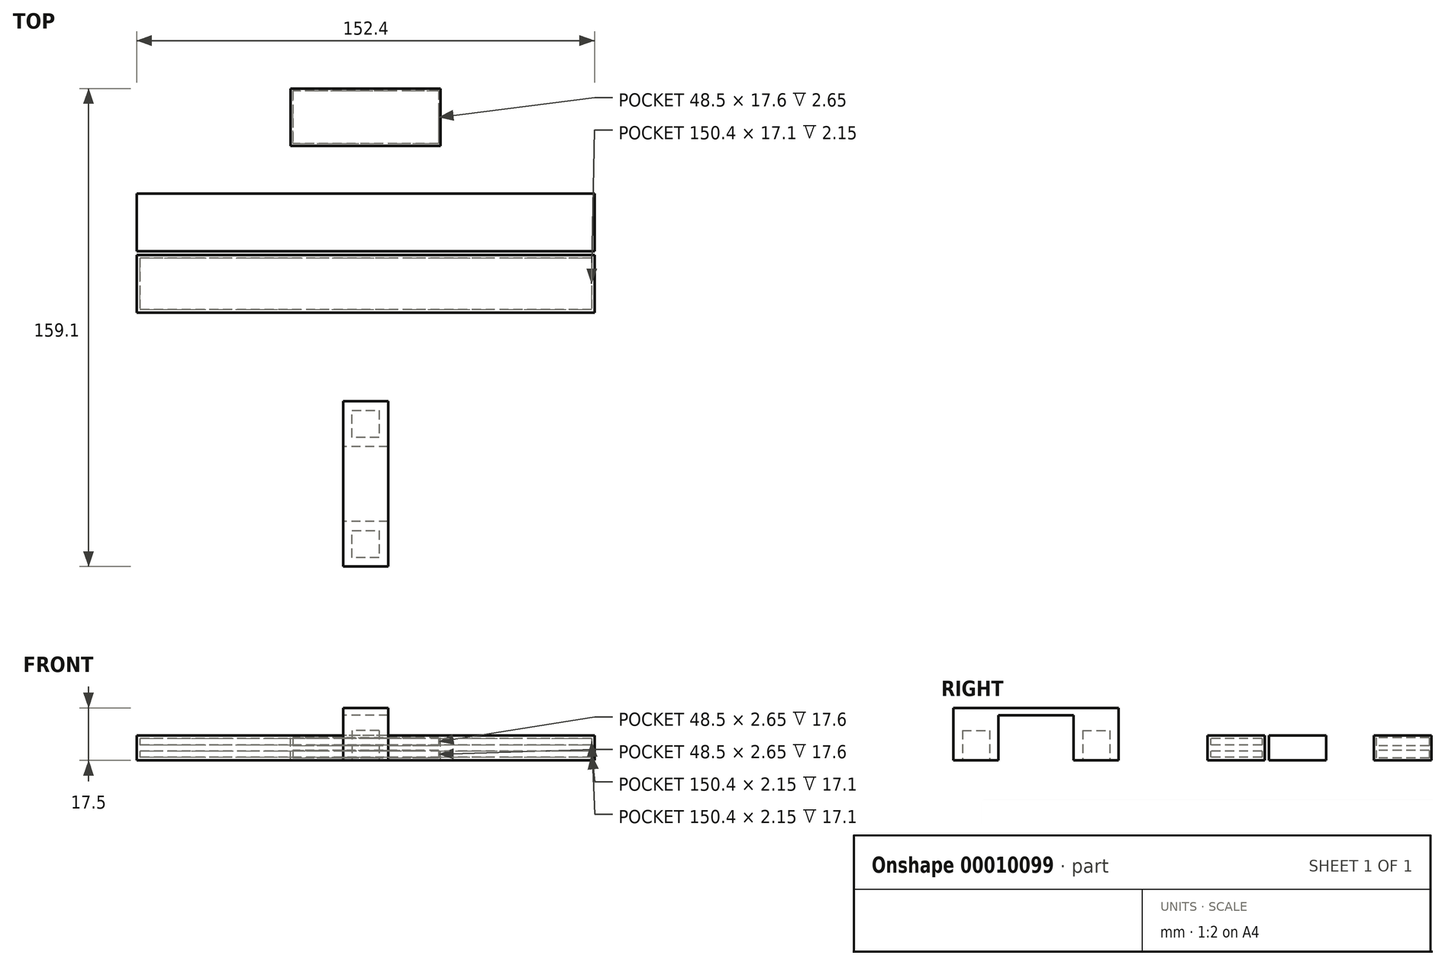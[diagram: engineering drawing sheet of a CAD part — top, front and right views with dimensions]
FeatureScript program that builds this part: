
annotation { "Feature Type Name" : "Feature", "Feature Type Description" : "" }
export const myFeature = defineFeature(function(context is Context, id is Id, definition is map)
    precondition{}
    {
        {
            var Q0;
            Q0=qCreatedBy(makeId("Right.planeOp"),FACE);
            var sketch = newSketch(context, id + "F0", { "sketchPlane" : qUnion([Q0])});
            skLineSegment(sketch, "E0.bottom", {"start": v(0, 0) * mm, "end": v(19.1, 0) * mm});
            skLineSegment(sketch, "E0.top", {"start": v(0, 8.3) * mm, "end": v(19.1, 8.3) * mm});
            skLineSegment(sketch, "E0.left", {"start": v(0, 0) * mm, "end": v(0, 8.3) * mm});
            skLineSegment(sketch, "E0.right", {"start": v(19.1, 0) * mm, "end": v(19.1, 8.3) * mm});
            skSolve(sketch);
        }
        {
            var Q0;
            Q0=makeQuery(id+"F0.imprint","IMPRINT",FACE,{"disambiguationData":[TD([[makeQuery(id+"F0.imprint","IMPRINT",EDGE,{"derivedFrom":sQuery(id+"F0.wireOp",EDGE,"E0.bottom")}),1.0]])]});
            extrude(context, id + "F1", {"entities" : qUnion([Q0]), "endBound" : BoundingType.SYMMETRIC, "depth" : 152.4 * mm});
        }
        {
            var Q0;
            Q0=qCreatedBy(makeId("Right.planeOp"),FACE);
            var sketch = newSketch(context, id + "F2", { "sketchPlane" : qUnion([Q0])});
            skLineSegment(sketch, "E1.bottom", {"start": v(-1.32, 0) * mm, "end": v(-20.42, 0) * mm});
            skLineSegment(sketch, "E1.top", {"start": v(-1.32, 8.3) * mm, "end": v(-20.42, 8.3) * mm});
            skLineSegment(sketch, "E1.left", {"start": v(-1.32, 0) * mm, "end": v(-1.32, 8.3) * mm});
            skLineSegment(sketch, "E1.right", {"start": v(-20.42, 0) * mm, "end": v(-20.42, 8.3) * mm});
            skLineSegment(sketch, "E2.bottom", {"start": v(-2.32, 7.3) * mm, "end": v(-19.42, 7.3) * mm});
            skLineSegment(sketch, "E2.top", {"start": v(-2.32, 1) * mm, "end": v(-19.42, 1) * mm});
            skLineSegment(sketch, "E2.left", {"start": v(-2.32, 7.3) * mm, "end": v(-2.32, 5.15) * mm});
            skLineSegment(sketch, "E2.right", {"start": v(-19.42, 7.3) * mm, "end": v(-19.42, 5.15) * mm});
            skLineSegment(sketch, "E3", {"start": v(-2.32, 5.15) * mm, "end": v(-19.42, 5.15) * mm});
            skLineSegment(sketch, "E4", {"start": v(-2.32, 3.15) * mm, "end": v(-19.42, 3.15) * mm});
            skLineSegment(sketch, "E5.trimOffspring", {"start": v(-2.32, 3.15) * mm, "end": v(-2.32, 1) * mm});
            skLineSegment(sketch, "E6.trimOffspring", {"start": v(-19.42, 3.15) * mm, "end": v(-19.42, 1) * mm});
            skSolve(sketch);
        }
        {
            var Q0;
            Q0=makeQuery(id+"F2.imprint","IMPRINT",FACE,{"disambiguationData":[TD([[makeQuery(id+"F2.imprint","IMPRINT",EDGE,{"derivedFrom":sQuery(id+"F2.wireOp",EDGE,"E1.bottom")}),-1.0]])]});
            extrude(context, id + "F3", {"entities" : qUnion([Q0]), "endBound" : BoundingType.SYMMETRIC, "depth" : 150.4 * mm});
        }
        {
            var Q0;
            Q0=makeQuery(id+"F3.opExtrude","CAP_FACE",FACE,{"disambiguationData":[OSD([sQuery(id+"F2.wireOp",EDGE,"E1.bottom"),sQuery(id+"F2.wireOp",EDGE,"E1.top"),sQuery(id+"F2.wireOp",EDGE,"E1.left"),sQuery(id+"F2.wireOp",EDGE,"E1.right"),sQuery(id+"F2.wireOp",EDGE,"E2.bottom"),sQuery(id+"F2.wireOp",EDGE,"E2.top"),sQuery(id+"F2.wireOp",EDGE,"E2.left"),sQuery(id+"F2.wireOp",EDGE,"E2.right"),sQuery(id+"F2.wireOp",EDGE,"E3"),sQuery(id+"F2.wireOp",EDGE,"E4"),sQuery(id+"F2.wireOp",EDGE,"E5.trimOffspring"),sQuery(id+"F2.wireOp",EDGE,"E6.trimOffspring")])],"isStart":true});
            var sketch = newSketch(context, id + "F4", { "sketchPlane" : qUnion([Q0])});
            skSolve(sketch);
        }
        {
            var Q0;
            Q0=makeQuery(id+"F4.imprint","IMPRINT",FACE,{"disambiguationData":[TD([[makeQuery(id+"F4.imprint","IMPRINT",EDGE,{"derivedFrom":makeQuery(id+"F3.opExtrude","CAP_EDGE",EDGE,{"disambiguationData":[OSD([sQuery(id+"F2.wireOp",EDGE,"E1.bottom")])],"isStart":true})}),1.0]])]});
            var Q1;
            Q1=makeQuery(id+"F4.imprint","IMPRINT",FACE,{"disambiguationData":[TD([[makeQuery(id+"F4.imprint","IMPRINT",EDGE,{"derivedFrom":makeQuery(id+"F3.opExtrude","CAP_EDGE",EDGE,{"disambiguationData":[OSD([sQuery(id+"F2.wireOp",EDGE,"E2.bottom")])],"isStart":true})}),-1.0]])]});
            var Q2;
            Q2=makeQuery(id+"F4.imprint","IMPRINT",FACE,{"disambiguationData":[TD([[makeQuery(id+"F4.imprint","IMPRINT",EDGE,{"derivedFrom":makeQuery(id+"F3.opExtrude","CAP_EDGE",EDGE,{"disambiguationData":[OSD([sQuery(id+"F2.wireOp",EDGE,"E2.top")])],"isStart":true})}),1.0]])]});
            extrude(context, id + "F5", {"entities" : qUnion([Q0, Q1, Q2]), "operationType" : NewBodyOperationType.ADD, "depth" : 1 * mm});
        }
        {
            var Q0;
            Q0=makeQuery(id+"F3.opExtrude","CAP_FACE",FACE,{"disambiguationData":[OSD([sQuery(id+"F2.wireOp",EDGE,"E1.bottom"),sQuery(id+"F2.wireOp",EDGE,"E1.top"),sQuery(id+"F2.wireOp",EDGE,"E1.left"),sQuery(id+"F2.wireOp",EDGE,"E1.right"),sQuery(id+"F2.wireOp",EDGE,"E2.bottom"),sQuery(id+"F2.wireOp",EDGE,"E2.top"),sQuery(id+"F2.wireOp",EDGE,"E2.left"),sQuery(id+"F2.wireOp",EDGE,"E2.right"),sQuery(id+"F2.wireOp",EDGE,"E3"),sQuery(id+"F2.wireOp",EDGE,"E4"),sQuery(id+"F2.wireOp",EDGE,"E5.trimOffspring"),sQuery(id+"F2.wireOp",EDGE,"E6.trimOffspring")])],"isStart":false});
            var sketch = newSketch(context, id + "F6", { "sketchPlane" : qUnion([Q0])});
            skSolve(sketch);
        }
        {
            var Q0;
            Q0=makeQuery(id+"F6.imprint","IMPRINT",FACE,{"disambiguationData":[TD([[makeQuery(id+"F6.imprint","IMPRINT",EDGE,{"derivedFrom":makeQuery(id+"F3.opExtrude","CAP_EDGE",EDGE,{"disambiguationData":[OSD([sQuery(id+"F2.wireOp",EDGE,"E1.bottom")])],"isStart":false})}),-1.0]])]});
            var Q1;
            Q1=makeQuery(id+"F6.imprint","IMPRINT",FACE,{"disambiguationData":[TD([[makeQuery(id+"F6.imprint","IMPRINT",EDGE,{"derivedFrom":makeQuery(id+"F3.opExtrude","CAP_EDGE",EDGE,{"disambiguationData":[OSD([sQuery(id+"F2.wireOp",EDGE,"E2.top")])],"isStart":false})}),-1.0]])]});
            var Q2;
            Q2=makeQuery(id+"F6.imprint","IMPRINT",FACE,{"disambiguationData":[TD([[makeQuery(id+"F6.imprint","IMPRINT",EDGE,{"derivedFrom":makeQuery(id+"F3.opExtrude","CAP_EDGE",EDGE,{"disambiguationData":[OSD([sQuery(id+"F2.wireOp",EDGE,"E2.bottom")])],"isStart":false})}),1.0]])]});
            extrude(context, id + "F7", {"entities" : qUnion([Q0, Q1, Q2]), "operationType" : NewBodyOperationType.ADD, "depth" : 1 * mm});
        }
        {
            var Q0;
            Q0=qCreatedBy(makeId("Right.planeOp"),FACE);
            var sketch = newSketch(context, id + "F8", { "sketchPlane" : qUnion([Q0])});
            skLineSegment(sketch, "E7", {"start": v(0, 0) * mm, "end": v(35, 0) * mm, "construction": true});
            skLineSegment(sketch, "E8.bottom", {"start": v(35, 0) * mm, "end": v(54.1, 0) * mm});
            skLineSegment(sketch, "E8.top", {"start": v(35, 8.3) * mm, "end": v(54.1, 8.3) * mm});
            skLineSegment(sketch, "E8.left", {"start": v(35, 0) * mm, "end": v(35, 8.3) * mm});
            skLineSegment(sketch, "E8.right", {"start": v(54.1, 0) * mm, "end": v(54.1, 8.3) * mm});
            skLineSegment(sketch, "E9.bottom", {"start": v(53.35, 7.55) * mm, "end": v(35.75, 7.55) * mm});
            skLineSegment(sketch, "E9.top", {"start": v(53.35, 0.75) * mm, "end": v(35.75, 0.75) * mm});
            skLineSegment(sketch, "E9.left", {"start": v(53.35, 7.55) * mm, "end": v(53.35, 4.9) * mm});
            skLineSegment(sketch, "E9.right", {"start": v(35.75, 7.55) * mm, "end": v(35.75, 4.9) * mm});
            skLineSegment(sketch, "E10", {"start": v(53.35, 4.9) * mm, "end": v(35.75, 4.9) * mm});
            skLineSegment(sketch, "E11", {"start": v(53.35, 4.15) * mm, "end": v(35.75, 4.15) * mm, "construction": true});
            skLineSegment(sketch, "E12", {"start": v(53.35, 3.4) * mm, "end": v(35.75, 3.4) * mm});
            skLineSegment(sketch, "E13.trimOffspring", {"start": v(35.75, 3.4) * mm, "end": v(35.75, 0.75) * mm});
            skLineSegment(sketch, "E14.trimOffspring", {"start": v(53.35, 3.4) * mm, "end": v(53.35, 0.75) * mm});
            skSolve(sketch);
        }
        {
            var Q0;
            Q0=makeQuery(id+"F8.imprint","IMPRINT",FACE,{"disambiguationData":[TD([[makeQuery(id+"F8.imprint","IMPRINT",EDGE,{"derivedFrom":sQuery(id+"F8.wireOp",EDGE,"E8.bottom")}),1.0]])]});
            extrude(context, id + "F9", {"entities" : qUnion([Q0]), "endBound" : BoundingType.SYMMETRIC, "depth" : 48.5 * mm});
        }
        {
            var Q0;
            Q0=makeQuery(id+"F9.opExtrude","CAP_FACE",FACE,{"disambiguationData":[OSD([sQuery(id+"F8.wireOp",EDGE,"E8.bottom"),sQuery(id+"F8.wireOp",EDGE,"E8.top"),sQuery(id+"F8.wireOp",EDGE,"E8.left"),sQuery(id+"F8.wireOp",EDGE,"E8.right"),sQuery(id+"F8.wireOp",EDGE,"E9.bottom"),sQuery(id+"F8.wireOp",EDGE,"E9.top"),sQuery(id+"F8.wireOp",EDGE,"E9.left"),sQuery(id+"F8.wireOp",EDGE,"E9.right"),sQuery(id+"F8.wireOp",EDGE,"E10"),sQuery(id+"F8.wireOp",EDGE,"E12"),sQuery(id+"F8.wireOp",EDGE,"E13.trimOffspring"),sQuery(id+"F8.wireOp",EDGE,"E14.trimOffspring")])],"isStart":true});
            var sketch = newSketch(context, id + "F10", { "sketchPlane" : qUnion([Q0])});
            skLineSegment(sketch, "E15.bottom", {"start": v(-54.1, 8.3) * mm, "end": v(-35, 8.3) * mm});
            skLineSegment(sketch, "E15.top", {"start": v(-54.1, 0) * mm, "end": v(-35, 0) * mm});
            skLineSegment(sketch, "E15.left", {"start": v(-54.1, 8.3) * mm, "end": v(-54.1, 0) * mm});
            skLineSegment(sketch, "E15.right", {"start": v(-35, 8.3) * mm, "end": v(-35, 0) * mm});
            skSolve(sketch);
        }
        {
            var Q0;
            Q0=makeQuery(id+"F10.imprint","IMPRINT",FACE,{"disambiguationData":[TD([[makeQuery(id+"F10.imprint","IMPRINT",EDGE,{"derivedFrom":sQuery(id+"F10.wireOp",EDGE,"E15.bottom")}),1.0]])]});
            var Q1;
            Q1=makeQuery(id+"F10.imprint","IMPRINT",FACE,{"disambiguationData":[TD([[makeQuery(id+"F10.imprint","IMPRINT",EDGE,{"derivedFrom":makeQuery(id+"F9.opExtrude","CAP_EDGE",EDGE,{"disambiguationData":[OSD([sQuery(id+"F8.wireOp",EDGE,"E9.bottom")])],"isStart":true})}),-1.0]])]});
            var Q2;
            Q2=makeQuery(id+"F10.imprint","IMPRINT",FACE,{"disambiguationData":[TD([[makeQuery(id+"F10.imprint","IMPRINT",EDGE,{"derivedFrom":makeQuery(id+"F9.opExtrude","CAP_EDGE",EDGE,{"disambiguationData":[OSD([sQuery(id+"F8.wireOp",EDGE,"E9.top")])],"isStart":true})}),1.0]])]});
            extrude(context, id + "F11", {"entities" : qUnion([Q0, Q1, Q2]), "operationType" : NewBodyOperationType.ADD, "depth" : 0.75 * mm});
        }
        {
            var Q0;
            Q0=makeQuery(id+"F9.opExtrude","CAP_FACE",FACE,{"disambiguationData":[OSD([sQuery(id+"F8.wireOp",EDGE,"E8.bottom"),sQuery(id+"F8.wireOp",EDGE,"E8.top"),sQuery(id+"F8.wireOp",EDGE,"E8.left"),sQuery(id+"F8.wireOp",EDGE,"E8.right"),sQuery(id+"F8.wireOp",EDGE,"E9.bottom"),sQuery(id+"F8.wireOp",EDGE,"E9.top"),sQuery(id+"F8.wireOp",EDGE,"E9.left"),sQuery(id+"F8.wireOp",EDGE,"E9.right"),sQuery(id+"F8.wireOp",EDGE,"E10"),sQuery(id+"F8.wireOp",EDGE,"E12"),sQuery(id+"F8.wireOp",EDGE,"E13.trimOffspring"),sQuery(id+"F8.wireOp",EDGE,"E14.trimOffspring")])],"isStart":false});
            var sketch = newSketch(context, id + "F12", { "sketchPlane" : qUnion([Q0])});
            skLineSegment(sketch, "E16.bottom", {"start": v(35, 8.3) * mm, "end": v(54.1, 8.3) * mm});
            skLineSegment(sketch, "E16.top", {"start": v(35, 0) * mm, "end": v(54.1, 0) * mm});
            skLineSegment(sketch, "E16.left", {"start": v(35, 8.3) * mm, "end": v(35, 0) * mm});
            skLineSegment(sketch, "E16.right", {"start": v(54.1, 8.3) * mm, "end": v(54.1, 0) * mm});
            skSolve(sketch);
        }
        {
            var Q0;
            Q0=makeQuery(id+"F12.imprint","IMPRINT",FACE,{"disambiguationData":[TD([[makeQuery(id+"F12.imprint","IMPRINT",EDGE,{"derivedFrom":sQuery(id+"F12.wireOp",EDGE,"E16.bottom")}),-1.0]])]});
            var Q1;
            Q1=makeQuery(id+"F12.imprint","IMPRINT",FACE,{"disambiguationData":[TD([[makeQuery(id+"F12.imprint","IMPRINT",EDGE,{"derivedFrom":makeQuery(id+"F9.opExtrude","CAP_EDGE",EDGE,{"disambiguationData":[OSD([sQuery(id+"F8.wireOp",EDGE,"E9.bottom")])],"isStart":false})}),1.0]])]});
            var Q2;
            Q2=makeQuery(id+"F12.imprint","IMPRINT",FACE,{"disambiguationData":[TD([[makeQuery(id+"F12.imprint","IMPRINT",EDGE,{"derivedFrom":makeQuery(id+"F9.opExtrude","CAP_EDGE",EDGE,{"disambiguationData":[OSD([sQuery(id+"F8.wireOp",EDGE,"E9.top")])],"isStart":false})}),-1.0]])]});
            extrude(context, id + "F13", {"entities" : qUnion([Q0, Q1, Q2]), "operationType" : NewBodyOperationType.ADD, "depth" : 0.75 * mm});
        }
        {
            var Q0;
            Q0=qCreatedBy(makeId("Right.planeOp"),FACE);
            var sketch = newSketch(context, id + "F14", { "sketchPlane" : qUnion([Q0])});
            skLineSegment(sketch, "E17", {"start": v(0, 0) * mm, "end": v(-50, 0) * mm, "construction": true});
            skLineSegment(sketch, "E18.bottom", {"start": v(-50, 0) * mm, "end": v(-65, 0) * mm});
            skLineSegment(sketch, "E18.top", {"start": v(-50, 15) * mm, "end": v(-65, 15) * mm});
            skLineSegment(sketch, "E18.left", {"start": v(-50, 0) * mm, "end": v(-50, 15) * mm});
            skLineSegment(sketch, "E18.right", {"start": v(-65, 0) * mm, "end": v(-65, 15) * mm});
            skLineSegment(sketch, "E19", {"start": v(-65, 15) * mm, "end": v(-90, 15) * mm});
            skLineSegment(sketch, "E20.bottom", {"start": v(-90, 15) * mm, "end": v(-105, 15) * mm});
            skLineSegment(sketch, "E20.top", {"start": v(-90, 0) * mm, "end": v(-105, 0) * mm});
            skLineSegment(sketch, "E20.left", {"start": v(-90, 15) * mm, "end": v(-90, 0) * mm});
            skLineSegment(sketch, "E20.right", {"start": v(-105, 15) * mm, "end": v(-105, 0) * mm});
            skLineSegment(sketch, "E21.bottom", {"start": v(-105, 15) * mm, "end": v(-50, 15) * mm});
            skLineSegment(sketch, "E21.top", {"start": v(-105, 17.5) * mm, "end": v(-50, 17.5) * mm});
            skLineSegment(sketch, "E21.left", {"start": v(-105, 15) * mm, "end": v(-105, 17.5) * mm});
            skLineSegment(sketch, "E21.right", {"start": v(-50, 15) * mm, "end": v(-50, 17.5) * mm});
            skSolve(sketch);
        }
        {
            var Q0;
            Q0=makeQuery(id+"F14.imprint","IMPRINT",FACE,{"disambiguationData":[TD([[makeQuery(id+"F14.imprint","IMPRINT",EDGE,{"derivedFrom":sQuery(id+"F14.wireOp",EDGE,"E20.top")}),-1.0]])]});
            var Q1;
            Q1=makeQuery(id+"F14.imprint","IMPRINT",FACE,{"disambiguationData":[TD([[makeQuery(id+"F14.imprint","IMPRINT",EDGE,{"derivedFrom":sQuery(id+"F14.wireOp",EDGE,"E21.top")}),-1.0]])]});
            var Q2;
            Q2=makeQuery(id+"F14.imprint","IMPRINT",FACE,{"disambiguationData":[TD([[makeQuery(id+"F14.imprint","IMPRINT",EDGE,{"derivedFrom":sQuery(id+"F14.wireOp",EDGE,"E18.bottom")}),-1.0]])]});
            extrude(context, id + "F15", {"entities" : qUnion([Q0, Q1, Q2]), "endBound" : BoundingType.SYMMETRIC, "depth" : 15 * mm});
        }
        {
            var Q0;
            Q0=makeQuery(id+"F15.opExtrude","SWEPT_FACE",FACE,{"disambiguationData":[OSD([sQuery(id+"F14.wireOp",EDGE,"E20.top")])]});
            var sketch = newSketch(context, id + "F16", { "sketchPlane" : qUnion([Q0])});
            skLineSegment(sketch, "E22.0.0", {"start": v(-7.5, 105) * mm, "end": v(-7.5, 90) * mm});
            skLineSegment(sketch, "E22.0.1", {"start": v(-7.5, 90) * mm, "end": v(7.5, 90) * mm});
            skLineSegment(sketch, "E22.0.2", {"start": v(7.5, 90) * mm, "end": v(7.5, 105) * mm});
            skLineSegment(sketch, "E22.0.3", {"start": v(7.5, 105) * mm, "end": v(-7.5, 105) * mm});
            skLineSegment(sketch, "E23.0.0", {"start": v(-7.5, 65) * mm, "end": v(-7.5, 50) * mm});
            skLineSegment(sketch, "E23.0.1", {"start": v(-7.5, 50) * mm, "end": v(7.5, 50) * mm});
            skLineSegment(sketch, "E23.0.2", {"start": v(7.5, 50) * mm, "end": v(7.5, 65) * mm});
            skLineSegment(sketch, "E23.0.3", {"start": v(7.5, 65) * mm, "end": v(-7.5, 65) * mm});
            skLineSegment(sketch, "E24.0", {"start": v(-4.5, 102) * mm, "end": v(-4.5, 93) * mm});
            skLineSegment(sketch, "E24.1", {"start": v(4.5, 102) * mm, "end": v(-4.5, 102) * mm});
            skLineSegment(sketch, "E24.2", {"start": v(4.5, 93) * mm, "end": v(4.5, 102) * mm});
            skLineSegment(sketch, "E24.3", {"start": v(-4.5, 93) * mm, "end": v(4.5, 93) * mm});
            skLineSegment(sketch, "E25.0", {"start": v(-4.5, 62) * mm, "end": v(-4.5, 53) * mm});
            skLineSegment(sketch, "E25.1", {"start": v(4.5, 62) * mm, "end": v(-4.5, 62) * mm});
            skLineSegment(sketch, "E25.2", {"start": v(4.5, 53) * mm, "end": v(4.5, 62) * mm});
            skLineSegment(sketch, "E25.3", {"start": v(-4.5, 53) * mm, "end": v(4.5, 53) * mm});
            skSolve(sketch);
        }
        {
            var Q0;
            Q0=makeQuery(id+"F16.imprint","IMPRINT",FACE,{"disambiguationData":[TD([[makeQuery(id+"F16.imprint","IMPRINT",EDGE,{"derivedFrom":sQuery(id+"F16.wireOp",EDGE,"E24.0")}),1.0]])]});
            var Q1;
            Q1=makeQuery(id+"F16.imprint","IMPRINT",FACE,{"disambiguationData":[TD([[makeQuery(id+"F16.imprint","IMPRINT",EDGE,{"derivedFrom":sQuery(id+"F16.wireOp",EDGE,"E25.0")}),1.0]])]});
            extrude(context, id + "F17", {"entities" : qUnion([Q0, Q1]), "operationType" : NewBodyOperationType.REMOVE, "oppositeDirection" : true, "depth" : 10 * mm});
        }
    });
